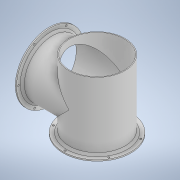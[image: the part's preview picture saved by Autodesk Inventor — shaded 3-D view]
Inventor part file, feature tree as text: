
AUTODESK INVENTOR PART (.ipt)
format: ipt  version: 2021 (Build 250183000, 183)  size: 304,640 bytes
history: native  units: mm
features: sketch x10, extrude x8, revolve x3, hole x3, plane x2, projected_geometry x2, fillet x1
ambient origin geometry x8: Origin, YZ Plane, XZ Plane, XY Plane, X Axis, Y Axis, Z Axis, Center Point
bodies: Solid1 (feature_tree)
feature tree (29):
  revolve  "Revolution1"  [1 undecoded]
  hole  "Hole1"  [1 undecoded]
  fillet  "Fillet1"  [1 undecoded]
  plane  "Work Plane1"
  sketch  "Sketch6"  dims[d10=16.0mm d11=3.0mm]
  extrude  "Extrusion3"  Depth=3.0mm
  extrude  "Extrusion5"  Depth=8.0mm
  extrude  "Extrusion4"  Depth=10.0mm
  revolve  "Revolution2"  [1 undecoded]
  extrude  "Extrusion6"  Depth=165.0mm
  hole  "Hole2"  [1 undecoded]
  extrude  "Extrusion7"  Depth=67.5mm TaperAngle=0.0deg
  plane  "Work Plane2"
  sketch  "Sketch12"  dims[d32=2.0mm d33=5.0mm]
  extrude  "Extrusion9"  Depth=67.5mm
  extrude  "Extrusion10"  TaperAngle=90.0deg  [1 undecoded]
  extrude  "Extrusion11"  Depth=67.5mm
  revolve  "Revolution3"  Angle=45.0deg
  hole  "Hole3"  [1 undecoded]
  sketch  "Sketch2"  dims[d3=90.0deg d5=81.5mm]
  projected_geometry  "Projected Loop1"
  sketch  "Sketch5"  dims[d7=9.0mm d8=5.0mm d9=45.0deg]
  projected_geometry  "Projected Loop6"
  sketch  "Sketch8"  dims[d16=4.5mm d17=8.0mm]
  sketch  "Sketch9"  dims[d18=60.0mm d20=360.0deg]
  sketch  "Sketch11"  dims[d22=4.5mm d23=10.0mm d24=9.4mm d25=2.0mm d26=90.0deg d27=13.0mm d28=20.594885mm d29=4.5mm]
  sketch  "Sketch14"  dims[d34=165.0mm d43=9.0mm]
  sketch  "Sketch15"  dims[d50=135.0mm d51=10.0mm d52=0.0mm]
  sketch  "Sketch16"  dims[d53=112.0mm d54=0.0mm d56=48.0mm d57=0.0mm d59=67.5mm d60=90.0deg d62=5.0mm d63=45.0deg d65=48.0mm d66=0.0mm d67=48.0mm d68=0.0mm d74=2.0mm d75=3.0mm d76=67.5mm d78=2.0mm d79=4.5mm d80=4.5mm d81=60.0mm d83=360.0deg d85=4.5mm d86=6.0mm d87=6.3mm d88=2.0mm d89=90.0deg d90=8.0mm d91=20.594885mm d92=75.0mm d93=135.0mm d95=72.0mm d96=10.0mm d97=0.0mm d98=35.0mm d99=0.0mm d100=2.0mm d101=48.0mm d102=0.0mm d103=9.0mm d105=5.0mm d106=45.0deg d107=3.0mm d109=67.5mm d110=67.5mm d111=90.0deg d112=4.5mm d113=4.5mm d114=60.0mm d116=360.0deg d118=4.5mm d119=6.0mm d120=9.4mm d121=2.0mm d122=90.0deg d123=8.0mm d124=20.594885mm]
note: 7 required parameter values undecoded (feature->parameter linkage not recoverable at this tier; creation-order binding heuristic only, values carry confidence <= 0.55)